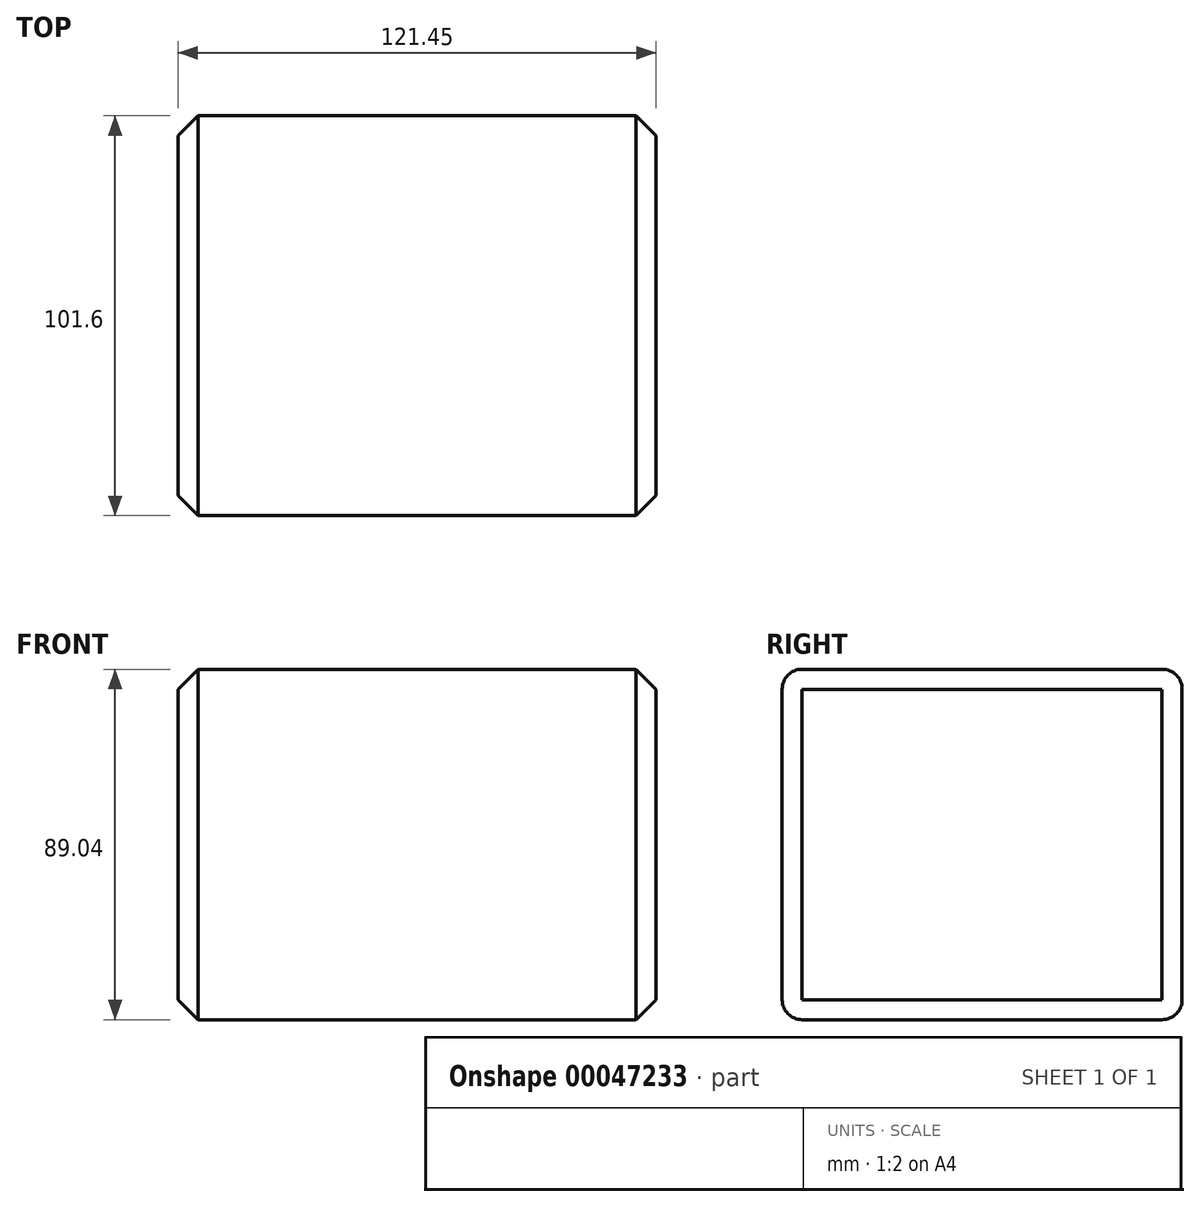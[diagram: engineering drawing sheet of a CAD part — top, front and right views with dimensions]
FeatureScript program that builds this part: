
annotation { "Feature Type Name" : "Feature", "Feature Type Description" : "" }
export const myFeature = defineFeature(function(context is Context, id is Id, definition is map)
    precondition{}
    {
        {
            var Q0;
            Q0=qCreatedBy(makeId("Front.planeOp"),FACE);
            var sketch = newSketch(context, id + "F0", { "sketchPlane" : qUnion([Q0])});
            skLineSegment(sketch, "E0.bottom", {"start": v(-61.48, 45.1) * mm, "end": v(59.97, 45.1) * mm});
            skLineSegment(sketch, "E0.top", {"start": v(-61.48, -43.94) * mm, "end": v(59.97, -43.94) * mm});
            skLineSegment(sketch, "E0.left", {"start": v(-61.48, 45.1) * mm, "end": v(-61.48, -43.94) * mm});
            skLineSegment(sketch, "E0.right", {"start": v(59.97, 45.1) * mm, "end": v(59.97, -43.94) * mm});
            skSolve(sketch);
        }
        {
            var Q0;
            Q0=makeQuery(id+"F0.imprint","IMPRINT",FACE,{"disambiguationData":[TD([[makeQuery(id+"F0.imprint","IMPRINT",EDGE,{"derivedFrom":sQuery(id+"F0.wireOp",EDGE,"E0.bottom")}),-1.0]])]});
            extrude(context, id + "F1", {"entities" : qUnion([Q0]), "depth" : 101.6 * mm});
        }
        {
            var Q0;
            Q0=makeQuery(id+"F1.opExtrude","CAP_EDGE",EDGE,{"disambiguationData":[OSD([sQuery(id+"F0.wireOp",EDGE,"E0.bottom")])],"isStart":true});
            var Q1;
            Q1=makeQuery(id+"F1.opExtrude","CAP_EDGE",EDGE,{"disambiguationData":[OSD([sQuery(id+"F0.wireOp",EDGE,"E0.bottom")])],"isStart":false});
            var Q2;
            Q2=makeQuery(id+"F1.opExtrude","CAP_EDGE",EDGE,{"disambiguationData":[OSD([sQuery(id+"F0.wireOp",EDGE,"E0.top")])],"isStart":true});
            var Q3;
            Q3=makeQuery(id+"F1.opExtrude","CAP_EDGE",EDGE,{"disambiguationData":[OSD([sQuery(id+"F0.wireOp",EDGE,"E0.top")])],"isStart":false});
            fillet(context, id + "F2", {"entities" : qUnion([Q0, Q1, Q2, Q3]), "radius" : 5.08 * mm, "tangentPropagation" : true, "allowEdgeOverflow" : false});
        }
        {
            var Q0;
            Q0=makeQuery(id+"F1.opExtrude","SWEPT_EDGE",EDGE,{"disambiguationData":[OSD([sQuery(id+"F0.wireOp",EDGE,"E0.top"),sQuery(id+"F0.wireOp",EDGE,"E0.right")])]});
            var Q1;
            Q1=makeQuery(id+"F1.opExtrude","SWEPT_EDGE",EDGE,{"disambiguationData":[OSD([sQuery(id+"F0.wireOp",EDGE,"E0.top"),sQuery(id+"F0.wireOp",EDGE,"E0.left")])]});
            var Q2;
            Q2=makeQuery(id+"F1.opExtrude","SWEPT_EDGE",EDGE,{"disambiguationData":[OSD([sQuery(id+"F0.wireOp",EDGE,"E0.bottom"),sQuery(id+"F0.wireOp",EDGE,"E0.right")])]});
            var Q3;
            Q3=makeQuery(id+"F1.opExtrude","SWEPT_EDGE",EDGE,{"disambiguationData":[OSD([sQuery(id+"F0.wireOp",EDGE,"E0.bottom"),sQuery(id+"F0.wireOp",EDGE,"E0.left")])]});
            chamfer(context, id + "F3", {"entities" : qUnion([Q0, Q1, Q2, Q3]), "width" : 5.08 * mm, "tangentPropagation" : true});
        }
    });
